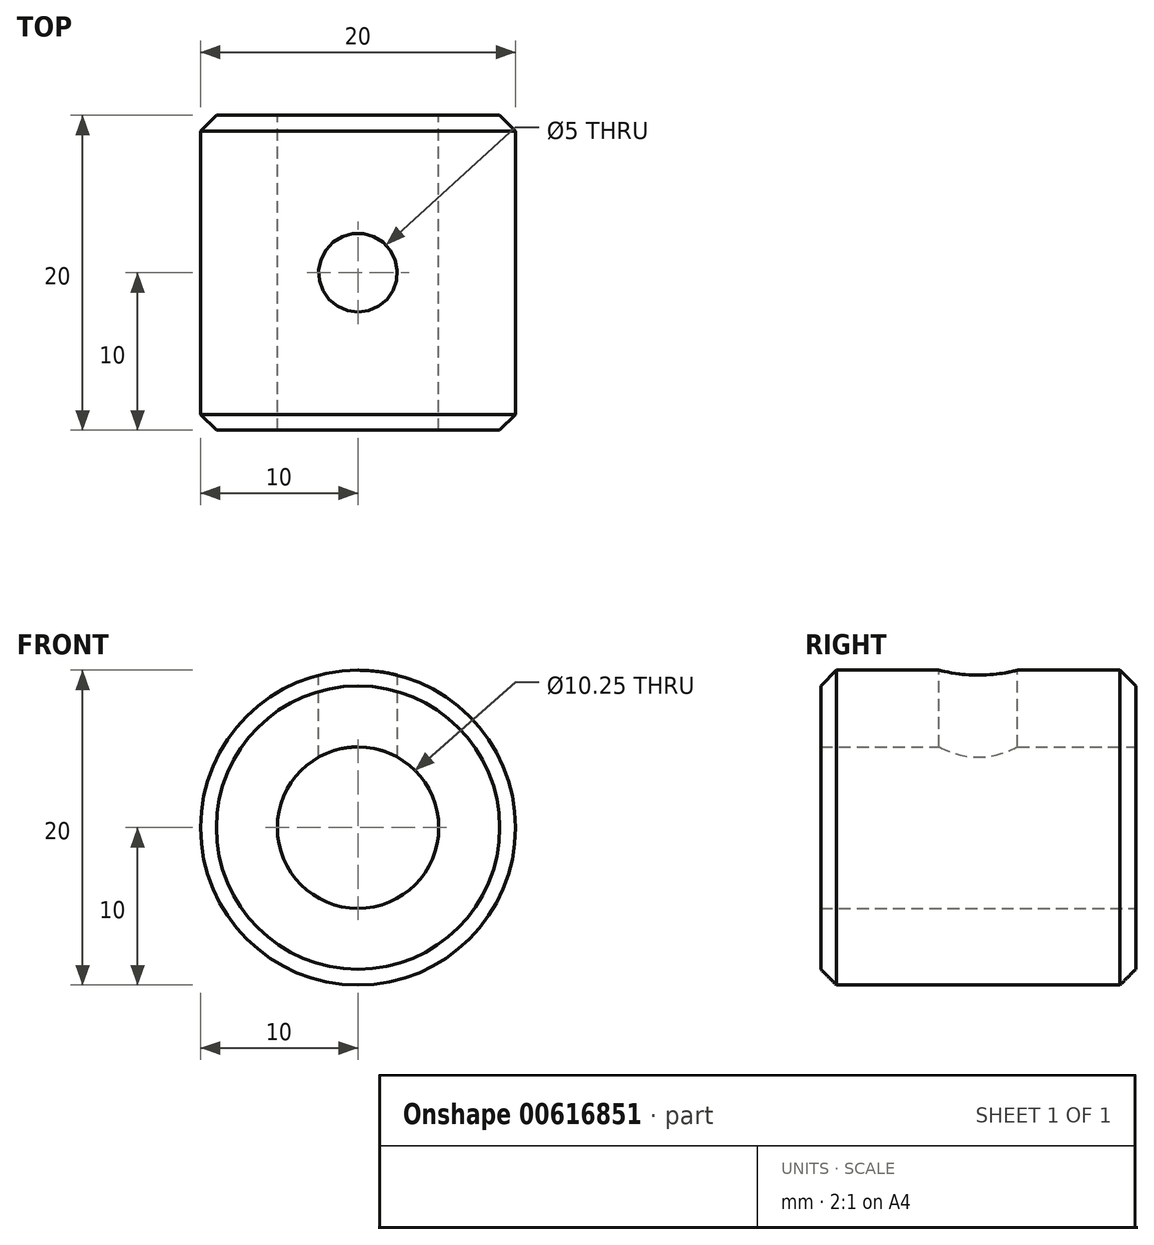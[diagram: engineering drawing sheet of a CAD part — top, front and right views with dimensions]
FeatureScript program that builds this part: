
annotation { "Feature Type Name" : "Feature", "Feature Type Description" : "" }
export const myFeature = defineFeature(function(context is Context, id is Id, definition is map)
    precondition{}
    {
        {
            var Q0;
            Q0=qCreatedBy(makeId("Front.planeOp"),FACE);
            var sketch = newSketch(context, id + "F0", { "sketchPlane" : qUnion([Q0])});
            skCircle(sketch, "E0", {"center": v(0, 0) * mm, "radius": 5.12 * mm});
            skCircle(sketch, "E1", {"center": v(0, 0) * mm, "radius": 10 * mm});
            skSolve(sketch);
        }
        {
            var Q0;
            Q0 = qSketchRegion(id + "F0", true);
            extrude(context, id + "F1", {"entities" : qUnion([Q0]), "depth" : 20 * mm, "offsetDistance" : 25 * mm});
        }
        {
            var Q0;
            Q0=qCreatedBy(makeId("Top.planeOp"),FACE);
            var sketch = newSketch(context, id + "F2", { "sketchPlane" : qUnion([Q0])});
            skLineSegment(sketch, "E2", {"start": v(10, 0) * mm, "end": v(10, -20) * mm, "construction": true});
            skLineSegment(sketch, "E3", {"start": v(-10, -20) * mm, "end": v(-10, 0) * mm, "construction": true});
            skLineSegment(sketch, "E4", {"start": v(-10, -10) * mm, "end": v(10, -10) * mm, "construction": true});
            skPoint(sketch, "E5", {"position": v(0, -10) * mm});
            skLineSegment(sketch, "E6", {"start": v(-10, 0) * mm, "end": v(10, 0) * mm, "construction": true});
            skLineSegment(sketch, "E7.0", {"start": v(10, -20) * mm, "end": v(-10, -20) * mm, "construction": true});
            skSolve(sketch);
        }
        {
            var Q0;
            Q0=sQuery(id+"F2.wireOp",VERTEX,"E5");
            var Q1;
            Q1=makeQuery(id+"F1.opExtrude","SWEPT_BODY",BODY,{"disambiguationData":[OSD([sQuery(id+"F0.wireOp",EDGE,"E0"),sQuery(id+"F0.wireOp",EDGE,"E1")])]});
            hole(context, id + "F3", {"style" : HoleStyle.SIMPLE, "endStyle" : HoleEndStyle.THROUGH, "oppositeDirection" : true, "standardTappedOrClearance" : lookupTablePath({ "standard" : "ISO", "engagement" : "75%", "pitch" : "1 mm", "size" : "M6", "type" : "Tapped" }), "standardBlindInLast" : lookupTablePath({ "standard" : "ISO", "engagement" : "75%", "pitch" : "1 mm", "size" : "M6", "type" : "Tapped" }), "holeDiameter" : 5 * mm, "majorDiameter" : 6 * mm, "showTappedDepth" : true, "isTappedThrough" : true, "tappedDepth" : 12 * mm, "tapClearance" : 3, "locations" : qUnion([Q0]), "scope" : qUnion([Q1]), "startStyle" : HoleStartStyle.PART});
        }
        {
            var Q0;
            Q0=makeQuery(id+"F1.opExtrude","CAP_EDGE",EDGE,{"disambiguationData":[OSD([sQuery(id+"F0.wireOp",EDGE,"E1")])],"isStart":false});
            var Q1;
            Q1=makeQuery(id+"F1.opExtrude","CAP_EDGE",EDGE,{"disambiguationData":[OSD([sQuery(id+"F0.wireOp",EDGE,"E1")])],"isStart":true});
            chamfer(context, id + "F4", {"entities" : qUnion([Q0, Q1]), "width" : 1 * mm, "tangentPropagation" : true});
        }
    });
